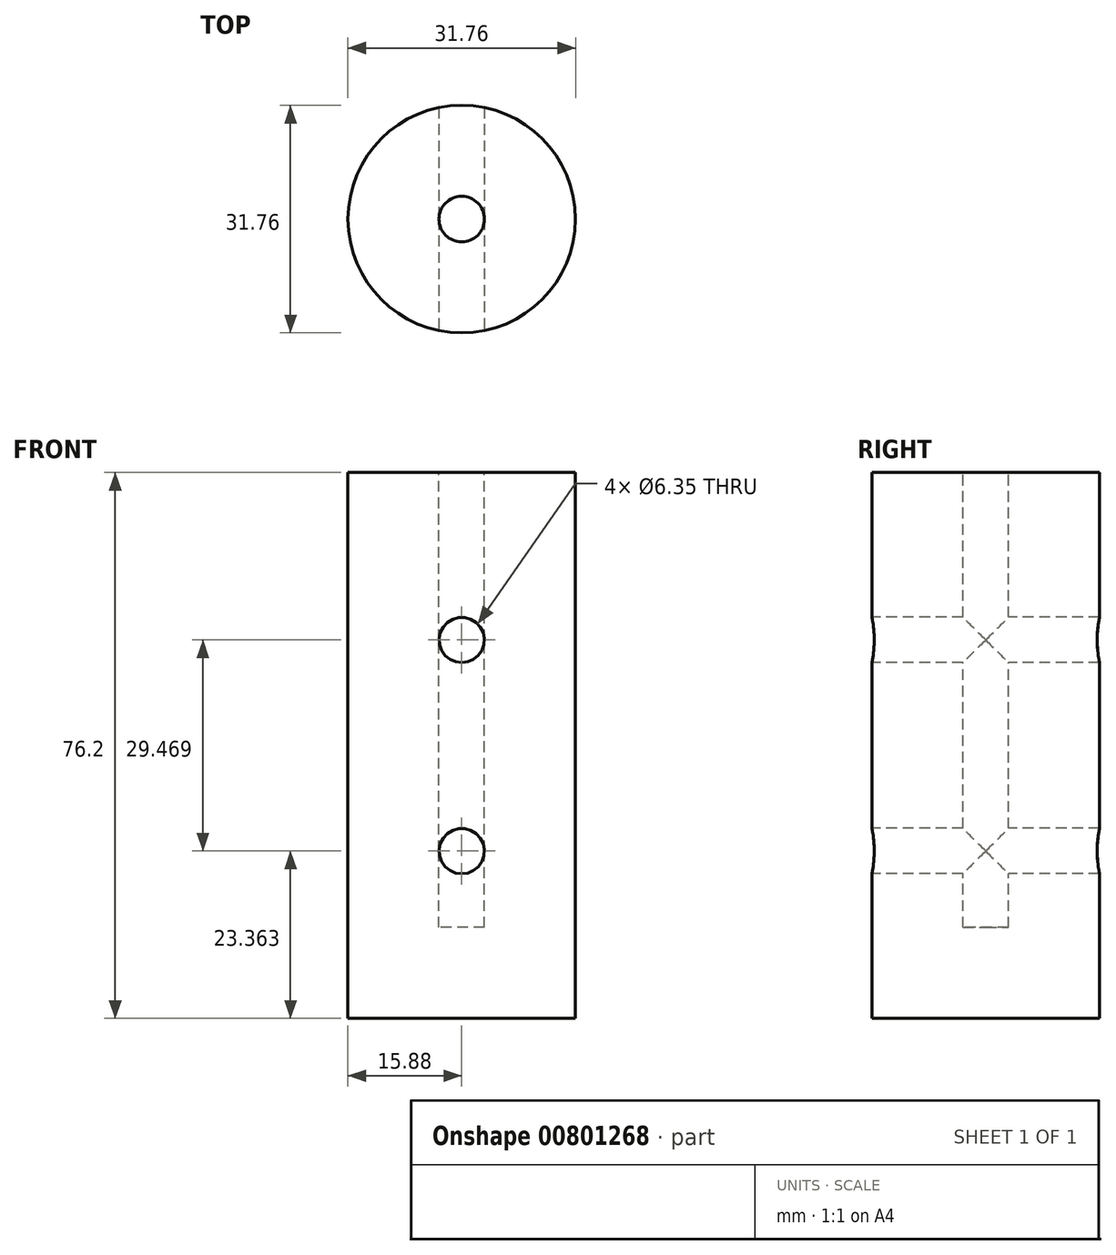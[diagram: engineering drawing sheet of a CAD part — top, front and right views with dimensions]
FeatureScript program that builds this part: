
annotation { "Feature Type Name" : "Feature", "Feature Type Description" : "" }
export const myFeature = defineFeature(function(context is Context, id is Id, definition is map)
    precondition{}
    {
        {
            var Q0;
            Q0=qCreatedBy(makeId("Top.planeOp"),FACE);
            var sketch = newSketch(context, id + "F0", { "sketchPlane" : qUnion([Q0])});
            skCircle(sketch, "E0", {"center": v(0, 0) * mm, "radius": 15.88 * mm});
            skSolve(sketch);
        }
        {
            var Q0;
            Q0 = qSketchRegion(id + "F0", true);
            extrude(context, id + "F1", {"entities" : qUnion([Q0]), "depth" : 76.2 * mm, "offsetDistance" : 25.4 * mm});
        }
        {
            var Q0;
            Q0=makeQuery(id+"F1.opExtrude","CAP_FACE",FACE,{"disambiguationData":[OSD([sQuery(id+"F0.wireOp",EDGE,"E0")])],"isStart":false});
            var sketch = newSketch(context, id + "F2", { "sketchPlane" : qUnion([Q0])});
            skCircle(sketch, "E1", {"center": v(0, 0) * mm, "radius": 3.18 * mm});
            skSolve(sketch);
        }
        {
            var Q0;
            Q0 = qSketchRegion(id + "F2", true);
            extrude(context, id + "F3", {"entities" : qUnion([Q0]), "operationType" : NewBodyOperationType.REMOVE, "oppositeDirection" : true, "depth" : 63.5 * mm, "offsetDistance" : 25.4 * mm});
        }
        {
            var Q0;
            Q0=qCreatedBy(makeId("Front.planeOp"),FACE);
            var sketch = newSketch(context, id + "F4", { "sketchPlane" : qUnion([Q0])});
            skCircle(sketch, "E2", {"center": v(0, 23.36) * mm, "radius": 3.18 * mm});
            skCircle(sketch, "E3", {"center": v(0, 52.83) * mm, "radius": 3.18 * mm});
            skSolve(sketch);
        }
        {
            var Q0;
            Q0 = qSketchRegion(id + "F4", true);
            extrude(context, id + "F5", {"entities" : qUnion([Q0]), "operationType" : NewBodyOperationType.REMOVE, "oppositeDirection" : true, "depth" : 50.8 * mm, "offsetDistance" : 25.4 * mm, "symmetric" : true});
        }
    });
